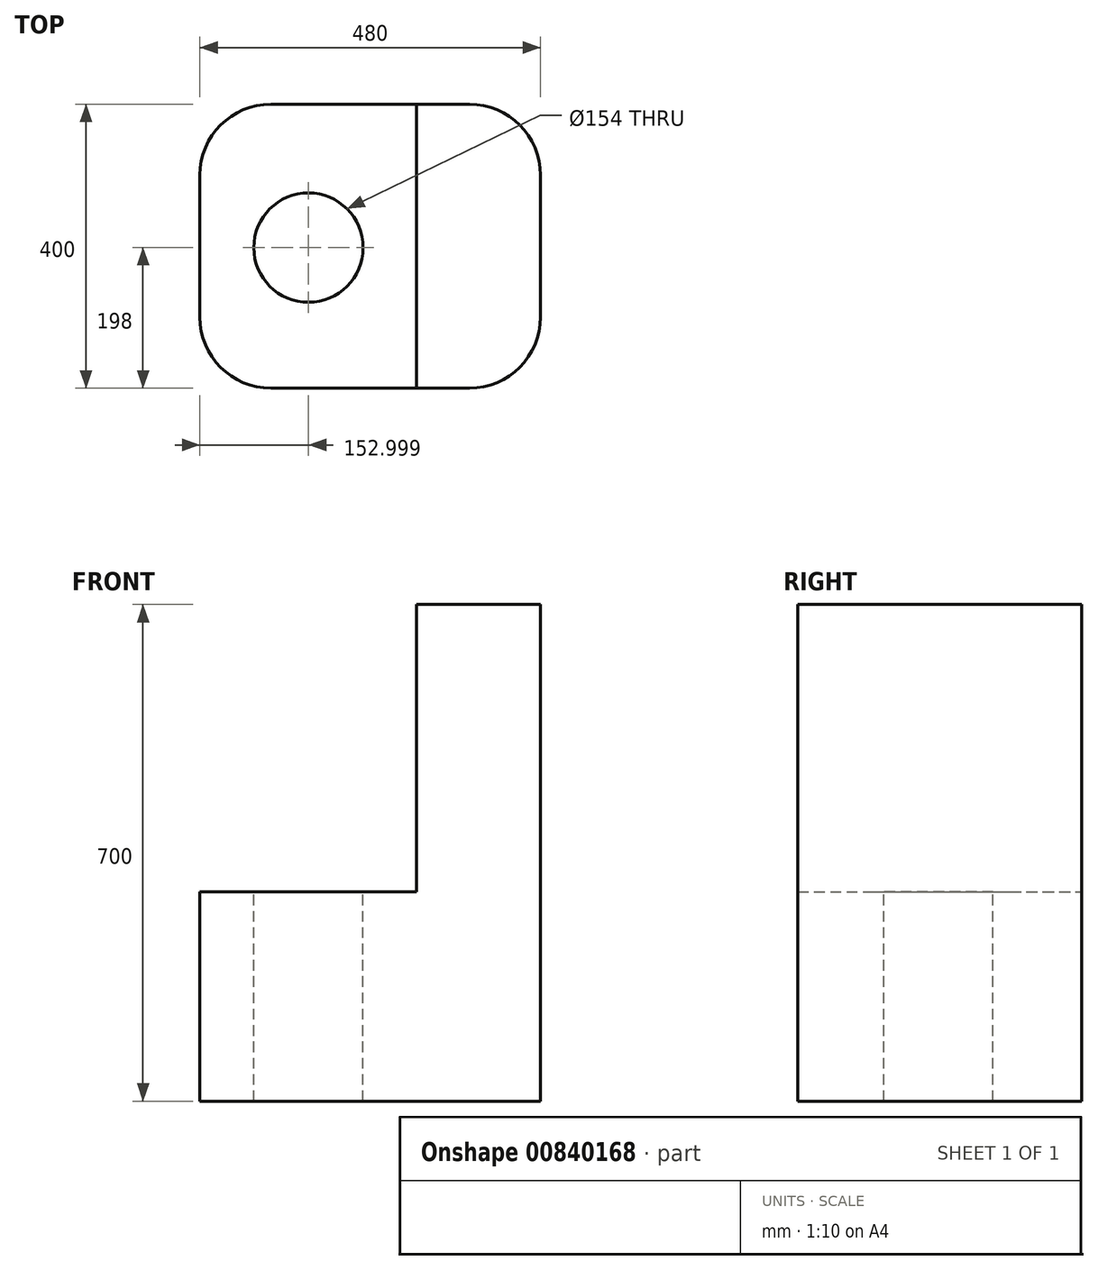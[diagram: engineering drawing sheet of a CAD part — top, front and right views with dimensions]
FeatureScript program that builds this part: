
annotation { "Feature Type Name" : "Feature", "Feature Type Description" : "" }
export const myFeature = defineFeature(function(context is Context, id is Id, definition is map)
    precondition{}
    {
        {
            var Q0;
            Q0=qCreatedBy(makeId("Front.planeOp"),FACE);
            var sketch = newSketch(context, id + "F0", { "sketchPlane" : qUnion([Q0])});
            skLineSegment(sketch, "E0", {"start": v(-235.24, 160.54) * mm, "end": v(-235.24, -134.46) * mm});
            skLineSegment(sketch, "E1", {"start": v(-235.24, -134.46) * mm, "end": v(244.76, -134.46) * mm});
            skLineSegment(sketch, "E2", {"start": v(244.76, -134.46) * mm, "end": v(244.76, 565.54) * mm});
            skLineSegment(sketch, "E3", {"start": v(244.76, 565.54) * mm, "end": v(69.76, 565.54) * mm});
            skLineSegment(sketch, "E4", {"start": v(69.76, 565.54) * mm, "end": v(69.76, 160.54) * mm});
            skLineSegment(sketch, "E5", {"start": v(69.76, 160.54) * mm, "end": v(-235.24, 160.54) * mm});
            skSolve(sketch);
        }
        {
            var Q0;
            Q0 = qSketchRegion(id + "F0", true);
            extrude(context, id + "F1", {"entities" : qUnion([Q0]), "depth" : 400 * mm, "offsetDistance" : 25 * mm});
        }
        {
            var Q0;
            Q0=makeQuery(id+"F1.opExtrude","SWEPT_FACE",FACE,{"disambiguationData":[OSD([sQuery(id+"F0.wireOp",EDGE,"E5")])]});
            var sketch = newSketch(context, id + "F2", { "sketchPlane" : qUnion([Q0])});
            skCircle(sketch, "E6", {"center": v(-82.24, -202) * mm, "radius": 77 * mm});
            skSolve(sketch);
        }
        {
            var Q0;
            Q0 = qSketchRegion(id + "F2", true);
            extrude(context, id + "F3", {"entities" : qUnion([Q0]), "operationType" : NewBodyOperationType.REMOVE, "endBound" : BoundingType.THROUGH_ALL, "oppositeDirection" : true, "depth" : 25 * mm, "offsetDistance" : 25 * mm});
        }
        {
            var Q0;
            Q0=makeQuery(id+"F1.opExtrude","CAP_EDGE",EDGE,{"disambiguationData":[OSD([sQuery(id+"F0.wireOp",EDGE,"E0")])],"isStart":true});
            var Q1;
            Q1=makeQuery(id+"F1.opExtrude","CAP_EDGE",EDGE,{"disambiguationData":[OSD([sQuery(id+"F0.wireOp",EDGE,"E0")])],"isStart":false});
            var Q2;
            Q2=makeQuery(id+"F1.opExtrude","CAP_EDGE",EDGE,{"disambiguationData":[OSD([sQuery(id+"F0.wireOp",EDGE,"E2")])],"isStart":false});
            var Q3;
            Q3=makeQuery(id+"F1.opExtrude","CAP_EDGE",EDGE,{"disambiguationData":[OSD([sQuery(id+"F0.wireOp",EDGE,"E2")])],"isStart":true});
            fillet(context, id + "F4", {"entities" : qUnion([Q0, Q1, Q2, Q3]), "radius" : 100 * mm, "tangentPropagation" : true, "allowEdgeOverflow" : false});
        }
    });
